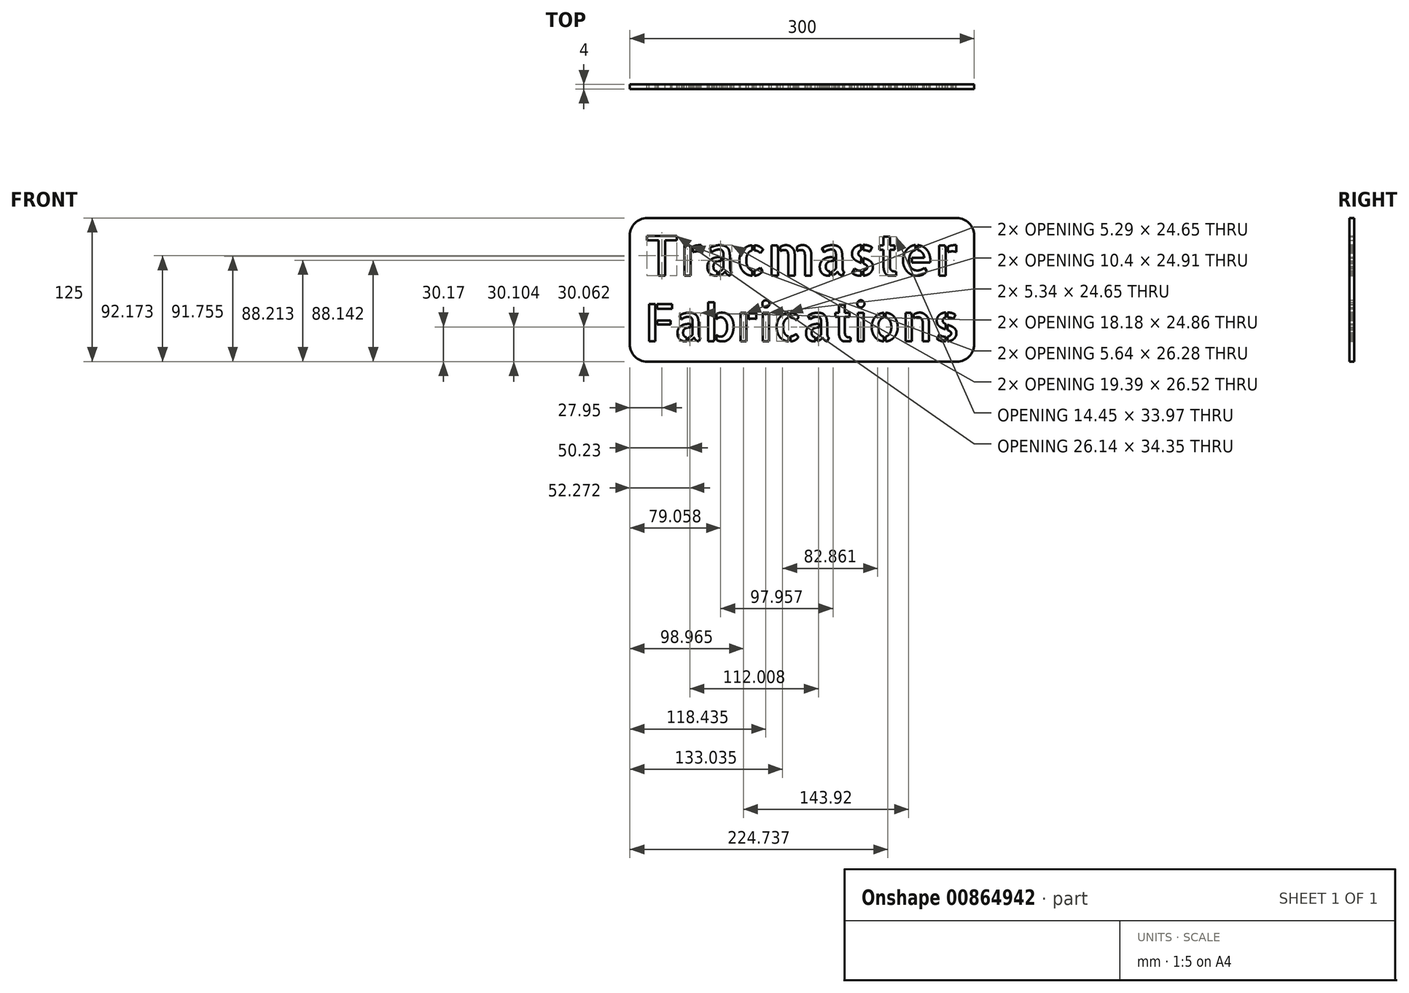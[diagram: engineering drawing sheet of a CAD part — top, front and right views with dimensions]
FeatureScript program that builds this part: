
annotation { "Feature Type Name" : "Feature", "Feature Type Description" : "" }
export const myFeature = defineFeature(function(context is Context, id is Id, definition is map)
    precondition{}
    {
        {
            var Q0;
            Q0=qCreatedBy(makeId("Front.planeOp"),FACE);
            var sketch = newSketch(context, id + "F0", { "sketchPlane" : qUnion([Q0])});
            skText(sketch, "E0", { "text": "Tracmaster", "fontName": "AllertaStencil-Regular.ttf"});
            skText(sketch, "E1", { "text": "Fabrications", "fontName": "AllertaStencil-Regular.ttf"});
            skLineSegment(sketch, "E2.bottom", {"start": v(135, -62.5) * mm, "end": v(-135, -62.5) * mm});
            skLineSegment(sketch, "E2.top", {"start": v(135, 62.5) * mm, "end": v(-135, 62.5) * mm});
            skLineSegment(sketch, "E2.left", {"start": v(150, -47.5) * mm, "end": v(150, 47.5) * mm});
            skLineSegment(sketch, "E2.right", {"start": v(-150, -47.5) * mm, "end": v(-150, 47.5) * mm});
            skPoint(sketch, "E2.middle", {"position": v(0, 0) * mm});
            skPoint(sketch, "E3.visualSharp", {"position": v(-150, 62.5) * mm});
            skArc(sketch, "E3.filletArc", {"start": v(-135, 62.5) * mm, "mid": v(-145.6, 58.1) * mm, "end": v(-150, 47.5) * mm});
            skPoint(sketch, "E4.visualSharp", {"position": v(150, 62.5) * mm});
            skArc(sketch, "E4.filletArc", {"start": v(150, 47.5) * mm, "mid": v(145.6, 58.1) * mm, "end": v(135, 62.5) * mm});
            skPoint(sketch, "E5.visualSharp", {"position": v(150, -62.5) * mm});
            skArc(sketch, "E5.filletArc", {"start": v(135, -62.5) * mm, "mid": v(145.6, -58.1) * mm, "end": v(150, -47.5) * mm});
            skPoint(sketch, "E6.visualSharp", {"position": v(-150, -62.5) * mm});
            skArc(sketch, "E6.filletArc", {"start": v(-150, -47.5) * mm, "mid": v(-145.6, -58.1) * mm, "end": v(-135, -62.5) * mm});
            const initialGuessF0  = {"E0": [-0.1375, 0.0125, 1, 0, 0.03436], "E1": [-0.1375, -0.04472, 1, 0, 0.03222]};
            skSetInitialGuess(sketch, initialGuessF0);
            skSolve(sketch);
        }
        {
            var Q0;
            Q0 = qSketchRegion(id + "F0", true);
            extrude(context, id + "F1", {"entities" : qUnion([Q0]), "depth" : 4 * mm, "offsetDistance" : 25 * mm});
        }
    });
